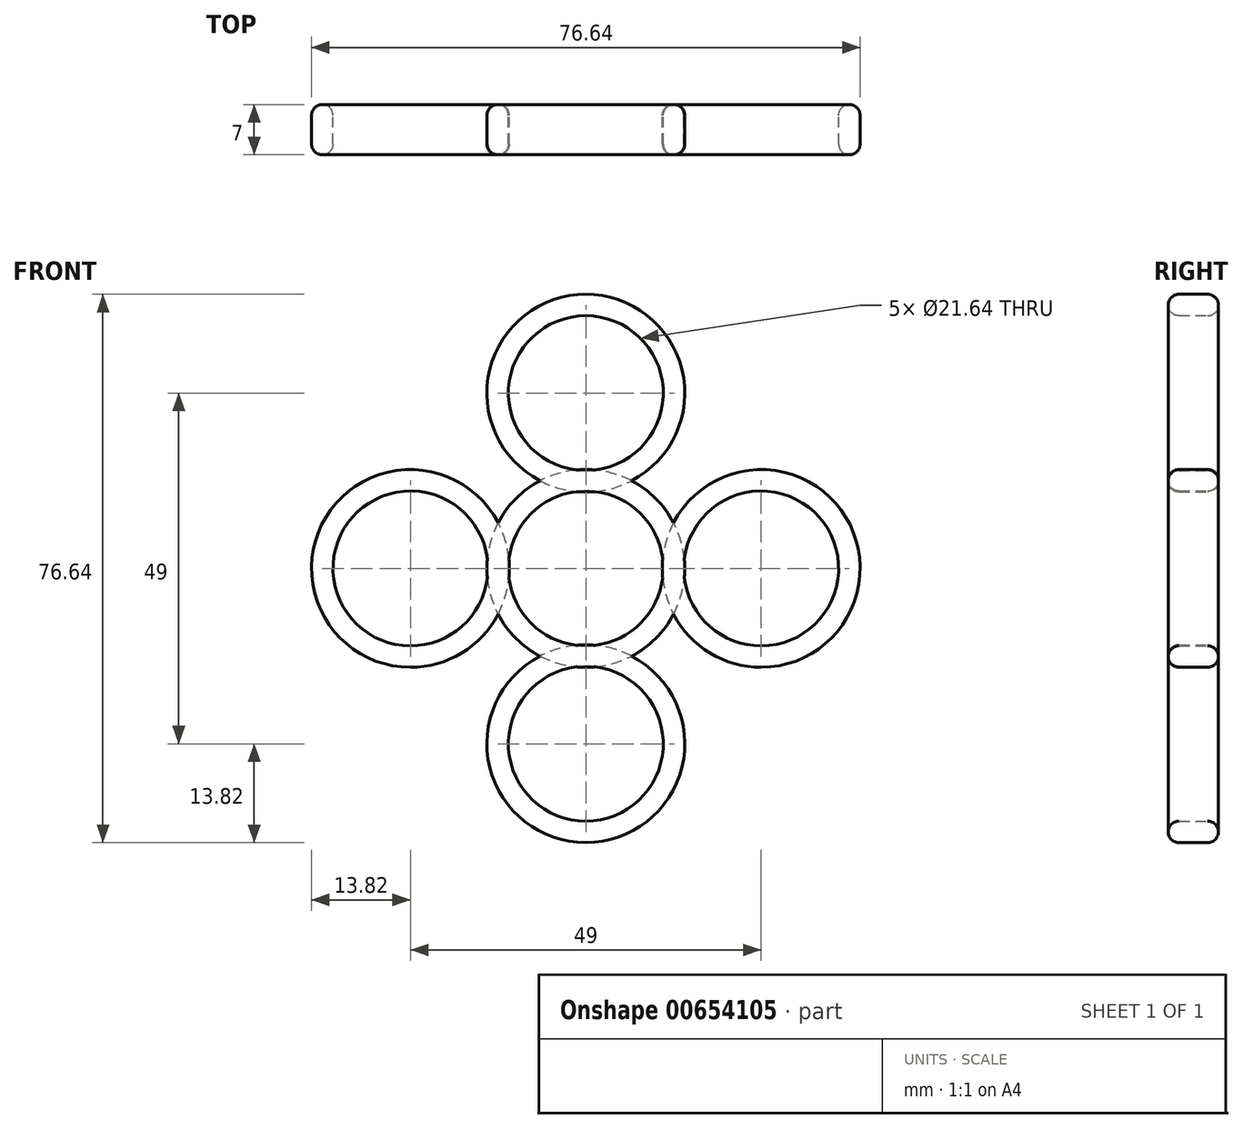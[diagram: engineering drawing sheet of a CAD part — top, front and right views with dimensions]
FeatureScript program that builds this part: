
annotation { "Feature Type Name" : "Feature", "Feature Type Description" : "" }
export const myFeature = defineFeature(function(context is Context, id is Id, definition is map)
    precondition{}
    {
        {
            var Q0;
            Q0=qCreatedBy(makeId("Front.planeOp"),FACE);
            var sketch = newSketch(context, id + "F0", { "sketchPlane" : qUnion([Q0])});
            skCircle(sketch, "E0", {"center": v(0, 0) * mm, "radius": 10.82 * mm});
            skCircle(sketch, "E1.0", {"center": v(0, 0) * mm, "radius": 13.82 * mm});
            skSolve(sketch);
        }
        {
            var Q0;
            Q0=makeQuery(id+"F0.imprint","IMPRINT",FACE,{"disambiguationData":[TD([[makeQuery(id+"F0.imprint","IMPRINT",EDGE,{"derivedFrom":sQuery(id+"F0.wireOp",EDGE,"E0")}),-1.0]])]});
            extrude(context, id + "F1", {"entities" : qUnion([Q0]), "depth" : 7 * mm, "offsetDistance" : 25 * mm});
        }
        {
            var Q0;
            Q0=makeQuery(id+"F1.opExtrude","CAP_EDGE",EDGE,{"disambiguationData":[OSD([sQuery(id+"F0.wireOp",EDGE,"E1.0")])],"isStart":false});
            var Q1;
            Q1=makeQuery(id+"F1.opExtrude","CAP_EDGE",EDGE,{"disambiguationData":[OSD([sQuery(id+"F0.wireOp",EDGE,"E0")])],"isStart":false});
            var Q2;
            Q2=makeQuery(id+"F1.opExtrude","SWEPT_FACE",FACE,{"disambiguationData":[OSD([sQuery(id+"F0.wireOp",EDGE,"E1.0")])]});
            fillet(context, id + "F2", {"entities" : qUnion([Q0, Q1, Q2]), "radius" : 1.5 * mm, "tangentPropagation" : true, "allowEdgeOverflow" : false});
        }
        {
            var Q0;
            Q0=makeQuery(id+"F1.opExtrude","CAP_EDGE",EDGE,{"disambiguationData":[OSD([sQuery(id+"F0.wireOp",EDGE,"E0")])],"isStart":false});
            var Q1;
            Q1=makeQuery(id+"F1.opExtrude","CAP_EDGE",EDGE,{"disambiguationData":[OSD([sQuery(id+"F0.wireOp",EDGE,"E1.0")])],"isStart":false});
            var Q2;
            Q2=makeQuery(id+"F1.opExtrude","CAP_EDGE",EDGE,{"disambiguationData":[OSD([sQuery(id+"F0.wireOp",EDGE,"E1.0")])],"isStart":true});
            var Q3;
            Q3=makeQuery(id+"F1.opExtrude","CAP_EDGE",EDGE,{"disambiguationData":[OSD([sQuery(id+"F0.wireOp",EDGE,"E0")])],"isStart":true});
            fillet(context, id + "F3", {"entities" : qUnion([Q0, Q1, Q2, Q3]), "radius" : 1.5 * mm, "tangentPropagation" : true, "allowEdgeOverflow" : false});
        }
        {
            var Q0;
            Q0=makeQuery(id+"F1.opExtrude","SWEPT_BODY",BODY,{"disambiguationData":[OSD([sQuery(id+"F0.wireOp",EDGE,"E0"),sQuery(id+"F0.wireOp",EDGE,"E1.0")])]});
            transform(context, id + "F4", {"entities" : qUnion([Q0]), "transformType" : TransformType.TRANSLATION_3D, "dx" : 24.5 * mm, "dy" : 0 * mm, "dz" : 0 * mm, "makeCopy" : true});
        }
        {
            var Q0;
            Q0=makeQuery(id+"F1.opExtrude","SWEPT_BODY",BODY,{"disambiguationData":[OSD([sQuery(id+"F0.wireOp",EDGE,"E0"),sQuery(id+"F0.wireOp",EDGE,"E1.0")])]});
            transform(context, id + "F5", {"entities" : qUnion([Q0]), "transformType" : TransformType.TRANSLATION_3D, "dx" : 0 * mm, "dy" : 0 * mm, "dz" : 24.5 * mm, "makeCopy" : true});
        }
        {
            var Q0;
            Q0=makeQuery(id+"F1.opExtrude","SWEPT_BODY",BODY,{"disambiguationData":[OSD([sQuery(id+"F0.wireOp",EDGE,"E0"),sQuery(id+"F0.wireOp",EDGE,"E1.0")])]});
            transform(context, id + "F6", {"entities" : qUnion([Q0]), "transformType" : TransformType.TRANSLATION_3D, "dx" : -24.5 * mm, "dy" : 0 * mm, "dz" : 0 * mm, "makeCopy" : true});
        }
        {
            var Q0;
            Q0=makeQuery(id+"F1.opExtrude","SWEPT_BODY",BODY,{"disambiguationData":[OSD([sQuery(id+"F0.wireOp",EDGE,"E0"),sQuery(id+"F0.wireOp",EDGE,"E1.0")])]});
            transform(context, id + "F7", {"entities" : qUnion([Q0]), "transformType" : TransformType.TRANSLATION_3D, "dx" : 0 * mm, "dy" : 0 * mm, "dz" : -24.5 * mm, "makeCopy" : true});
        }
    });
